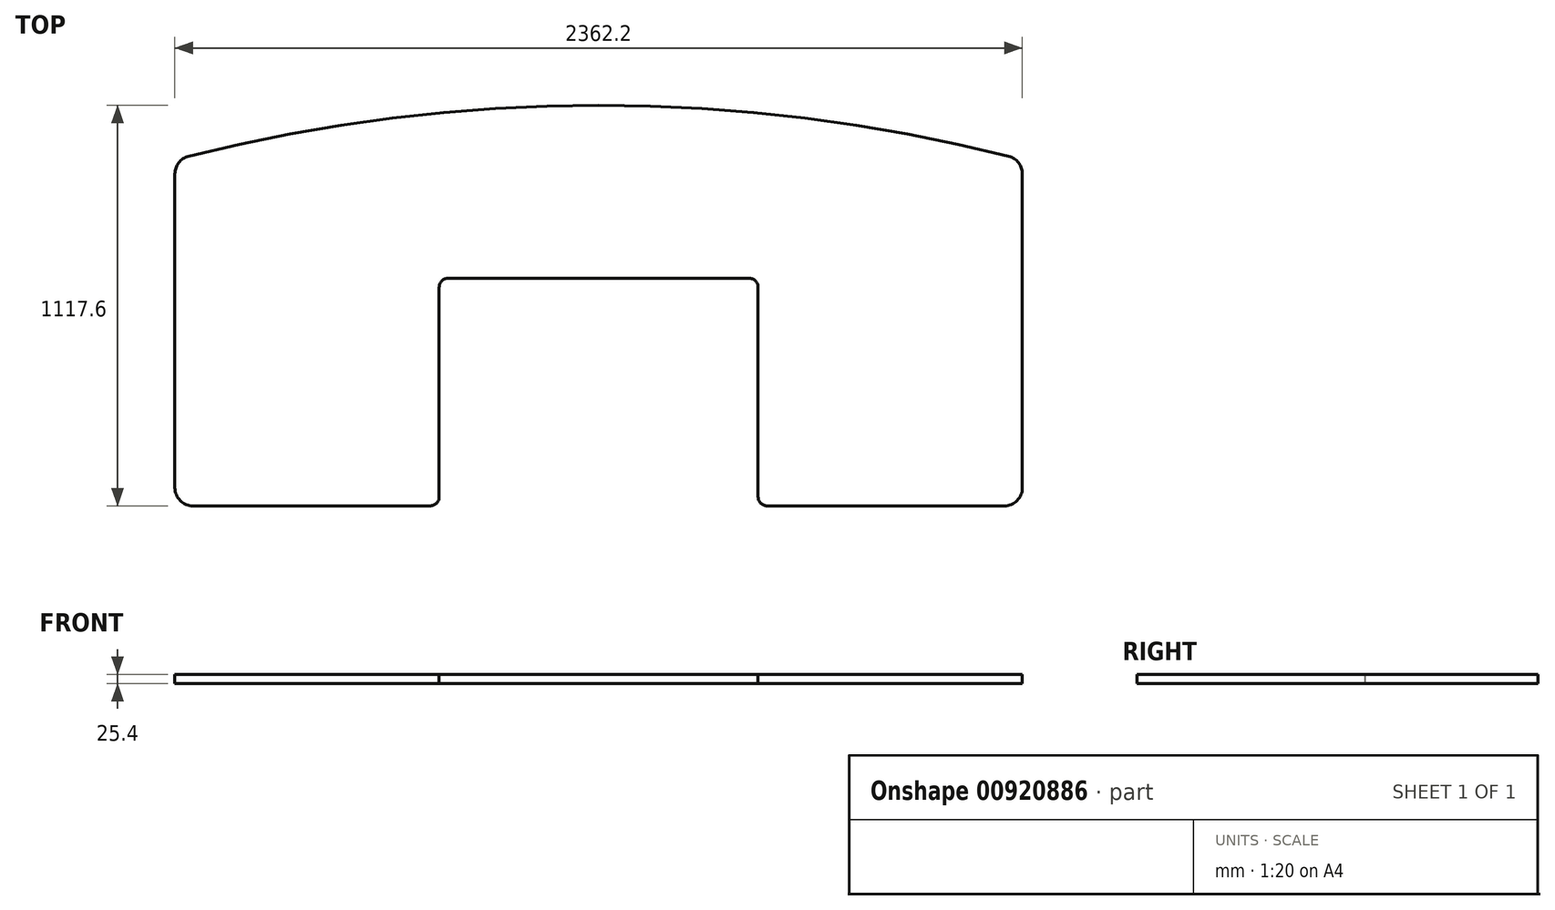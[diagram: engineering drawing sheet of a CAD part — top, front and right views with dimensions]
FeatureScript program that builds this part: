
annotation { "Feature Type Name" : "Feature", "Feature Type Description" : "" }
export const myFeature = defineFeature(function(context is Context, id is Id, definition is map)
    precondition{}
    {
        {
            var Q0;
            Q0=qCreatedBy(makeId("Top.planeOp"),FACE);
            var sketch = newSketch(context, id + "F0", { "sketchPlane" : qUnion([Q0])});
            skLineSegment(sketch, "E0.bottom", {"start": v(1130.3, -482.6) * mm, "end": v(469.9, -482.6) * mm});
            skLineSegment(sketch, "E0.left", {"start": v(1181.1, -431.8) * mm, "end": v(1181.1, 443.24) * mm});
            skLineSegment(sketch, "E0.right", {"start": v(-1181.1, -431.8) * mm, "end": v(-1181.1, 443.24) * mm});
            skPoint(sketch, "E0.middle", {"position": v(0, 0) * mm});
            skPoint(sketch, "E1.visualSharp", {"position": v(-1181.1, -482.6) * mm});
            skArc(sketch, "E1.filletArc", {"start": v(-1181.1, -431.8) * mm, "mid": v(-1166.22, -467.72) * mm, "end": v(-1130.3, -482.6) * mm});
            skPoint(sketch, "E2.visualSharp", {"position": v(1181.1, -482.6) * mm});
            skArc(sketch, "E2.filletArc", {"start": v(1130.3, -482.6) * mm, "mid": v(1166.22, -467.72) * mm, "end": v(1181.1, -431.8) * mm});
            skLineSegment(sketch, "E3", {"start": v(0, 482.6) * mm, "end": v(0, 635) * mm, "construction": true});
            skArc(sketch, "E4", {"start": v(1142.78, 492.48) * mm, "mid": v(0, 635) * mm, "end": v(-1142.78, 492.48) * mm});
            skPoint(sketch, "E5.visualSharp", {"position": v(-1181.1, 482.6) * mm});
            skArc(sketch, "E5.filletArc", {"start": v(-1142.78, 492.48) * mm, "mid": v(-1170.4, 474.44) * mm, "end": v(-1181.1, 443.24) * mm});
            skPoint(sketch, "E6.visualSharp", {"position": v(1181.1, 482.6) * mm});
            skArc(sketch, "E6.filletArc", {"start": v(1181.1, 443.24) * mm, "mid": v(1170.4, 474.44) * mm, "end": v(1142.78, 492.48) * mm});
            skLineSegment(sketch, "E7.top", {"start": v(-419.1, 152.4) * mm, "end": v(419.1, 152.4) * mm});
            skLineSegment(sketch, "E7.left", {"start": v(-444.5, -457.2) * mm, "end": v(-444.5, 127) * mm});
            skLineSegment(sketch, "E7.right", {"start": v(444.5, -457.2) * mm, "end": v(444.5, 127) * mm});
            skPoint(sketch, "E8.visualSharp", {"position": v(444.5, 152.4) * mm});
            skArc(sketch, "E8.filletArc", {"start": v(444.5, 127) * mm, "mid": v(437.06, 144.96) * mm, "end": v(419.1, 152.4) * mm});
            skPoint(sketch, "E9.visualSharp", {"position": v(-444.5, 152.4) * mm});
            skArc(sketch, "E9.filletArc", {"start": v(-419.1, 152.4) * mm, "mid": v(-437.06, 144.96) * mm, "end": v(-444.5, 127) * mm});
            skLineSegment(sketch, "E10.trimOffspring", {"start": v(-469.9, -482.6) * mm, "end": v(-1130.3, -482.6) * mm});
            skPoint(sketch, "E11.orphan", {"position": v(0, -482.6) * mm});
            skPoint(sketch, "E12.visualSharp", {"position": v(444.5, -482.6) * mm});
            skArc(sketch, "E12.filletArc", {"start": v(444.5, -457.2) * mm, "mid": v(451.94, -475.16) * mm, "end": v(469.9, -482.6) * mm});
            skLineSegment(sketch, "E13", {"start": v(0, -482.6) * mm, "end": v(0, -225.65) * mm});
            skPoint(sketch, "E14.visualSharp", {"position": v(-444.5, -482.6) * mm});
            skArc(sketch, "E14.filletArc", {"start": v(-469.9, -482.6) * mm, "mid": v(-451.94, -475.16) * mm, "end": v(-444.5, -457.2) * mm});
            skSolve(sketch);
        }
        {
            var Q0;
            Q0=makeQuery(id+"F0.imprint","IMPRINT",FACE,{"disambiguationData":[TD([[makeQuery(id+"F0.imprint","IMPRINT",EDGE,{"derivedFrom":sQuery(id+"F0.wireOp",EDGE,"E0.bottom")}),-1.0]])]});
            extrude(context, id + "F1", {"entities" : qUnion([Q0]), "depth" : 25.4 * mm, "offsetDistance" : 25.4 * mm});
        }
    });
